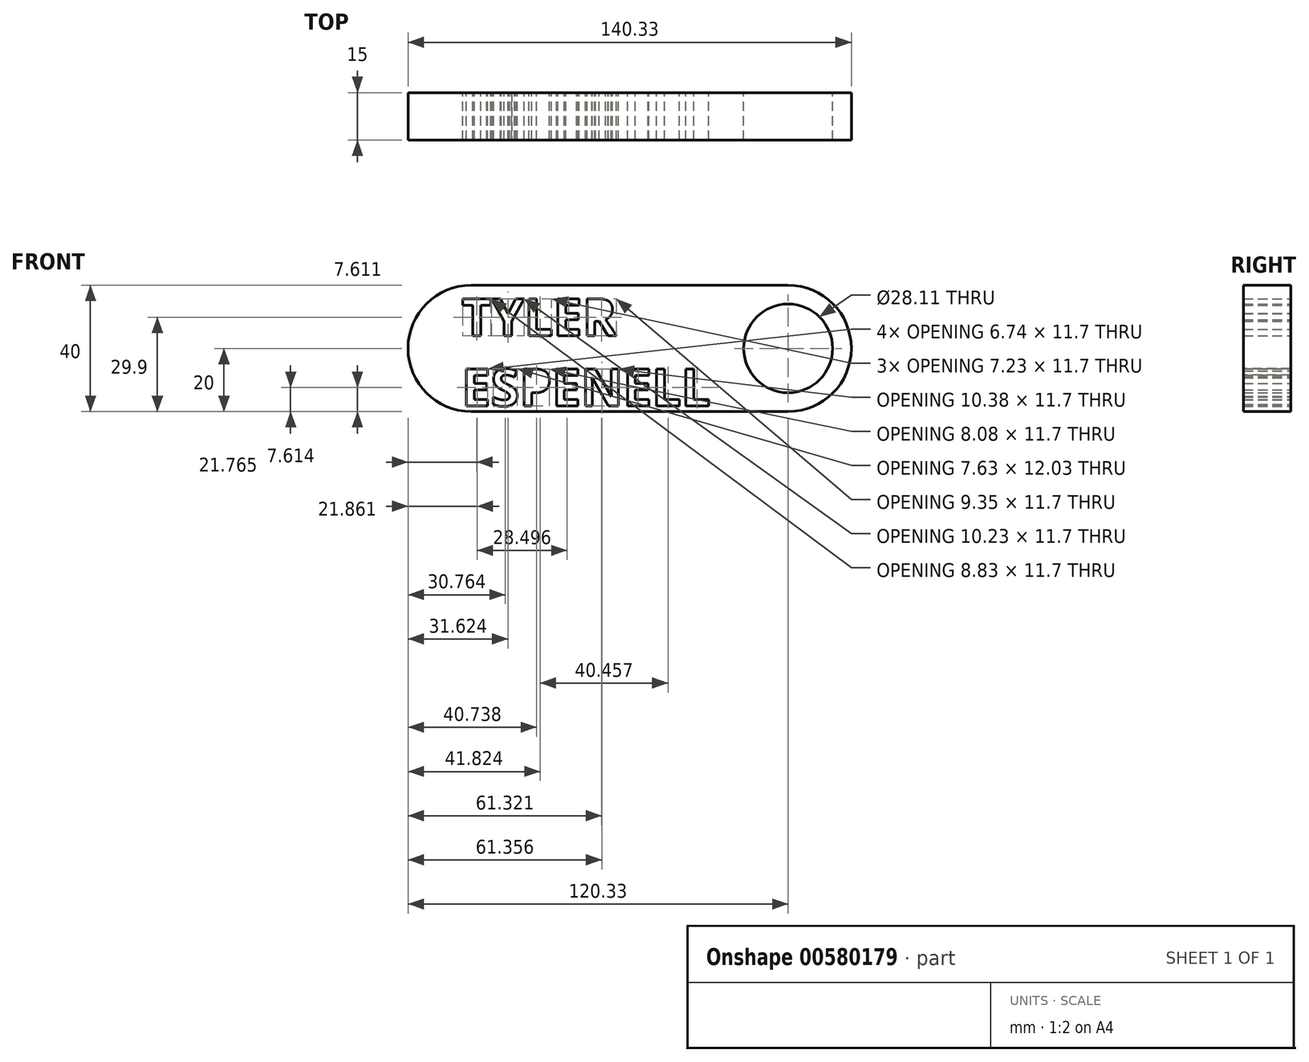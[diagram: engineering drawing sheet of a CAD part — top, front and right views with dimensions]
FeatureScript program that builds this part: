
annotation { "Feature Type Name" : "Feature", "Feature Type Description" : "" }
export const myFeature = defineFeature(function(context is Context, id is Id, definition is map)
    precondition{}
    {
        {
            var Q0;
            Q0=qCreatedBy(makeId("Front.planeOp"),FACE);
            var sketch = newSketch(context, id + "F0", { "sketchPlane" : qUnion([Q0])});
            skArc(sketch, "E0", {"start": v(-60.2, 20) * mm, "mid": v(-80.2, 0) * mm, "end": v(-60.2, -20) * mm});
            skArc(sketch, "E1", {"start": v(40.13, -20) * mm, "mid": v(60.13, 0) * mm, "end": v(40.13, 20) * mm});
            skLineSegment(sketch, "E2", {"start": v(-60.2, 20) * mm, "end": v(40.13, 20) * mm});
            skLineSegment(sketch, "E3", {"start": v(-60.2, -20) * mm, "end": v(40.13, -20) * mm});
            skText(sketch, "E4", { "text": "TYLER\nESPENELL", "fontName": "OpenSans-Bold.ttf"});
            skCircle(sketch, "E5", {"center": v(40.13, 0) * mm, "radius": 14.06 * mm});
            const initialGuessF0  = {"E4": [-0.06318, 0.00405, 1, 0, 0.0118]};
            skSetInitialGuess(sketch, initialGuessF0);
            skSolve(sketch);
        }
        {
            var Q0;
            Q0 = qSketchRegion(id + "F0", true);
            extrude(context, id + "F1", {"entities" : qUnion([Q0]), "depth" : 15 * mm, "offsetDistance" : 25 * mm});
        }
    });
